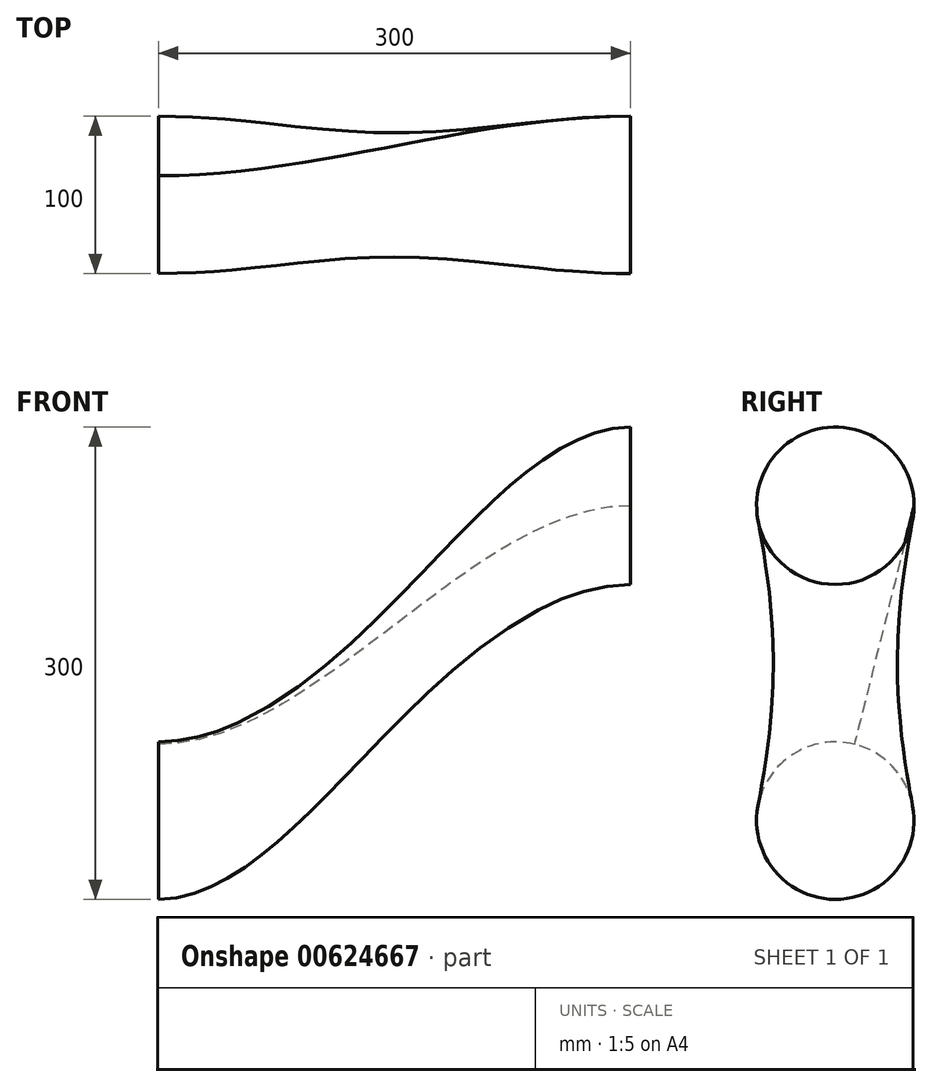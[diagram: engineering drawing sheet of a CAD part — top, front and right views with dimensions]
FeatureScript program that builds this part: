
annotation { "Feature Type Name" : "Feature", "Feature Type Description" : "" }
export const myFeature = defineFeature(function(context is Context, id is Id, definition is map)
    precondition{}
    {
        {
            var Q0;
            Q0=qCreatedBy(makeId("Right.planeOp"),FACE);
            var sketch = newSketch(context, id + "F0", { "sketchPlane" : qUnion([Q0])});
            skCircle(sketch, "E0", {"center": v(0, 0) * mm, "radius": 50 * mm});
            skSolve(sketch);
        }
        {
            var Q0;
            Q0=qCreatedBy(makeId("Right.planeOp"),FACE);
            cPlane(context, id + "F1", {"entities" : qUnion([Q0]), "cplaneType" : CPlaneType.OFFSET, "offset" : 300 * mm, "width" : 150 * mm, "height" : 150 * mm});
        }
        {
            var Q0;
            Q0=qCreatedBy(id+"F1.planeOp",FACE);
            var sketch = newSketch(context, id + "F2", { "sketchPlane" : qUnion([Q0])});
            skCircle(sketch, "E1", {"center": v(0, 200) * mm, "radius": 50 * mm});
            skSolve(sketch);
        }
        {
            var Q0;
            Q0=makeQuery(id+"F2.imprint","IMPRINT",FACE,{"disambiguationData":[TD([[makeQuery(id+"F2.imprint","IMPRINT",EDGE,{"derivedFrom":sQuery(id+"F2.wireOp",EDGE,"E1")}),1.0]])]});
            var Q1;
            Q1=makeQuery(id+"F0.imprint","IMPRINT",FACE,{"disambiguationData":[TD([[makeQuery(id+"F0.imprint","IMPRINT",EDGE,{"derivedFrom":sQuery(id+"F0.wireOp",EDGE,"E0")}),1.0]])]});
            var Q2;
            Q2=sQuery(id+"F2.wireOp",EDGE,"E1");
            var Q3;
            Q3=sQuery(id+"F0.wireOp",EDGE,"E0");
            loft(context, id + "F3", {"bodyType" : ToolBodyType.SURFACE, "startCondition" : LoftEndDerivativeType.NORMAL_TO_PROFILE, "startMagnitude" : 1, "endCondition" : LoftEndDerivativeType.NORMAL_TO_PROFILE, "endMagnitude" : 1, "sheetProfilesArray" : [{ "sheetProfileEntities" : qUnion([Q0]) }, { "sheetProfileEntities" : qUnion([Q1]) }], "wireProfilesArray" : [{ "wireProfileEntities" : qUnion([Q2]) }, { "wireProfileEntities" : qUnion([Q3]) }]});
        }
    });
